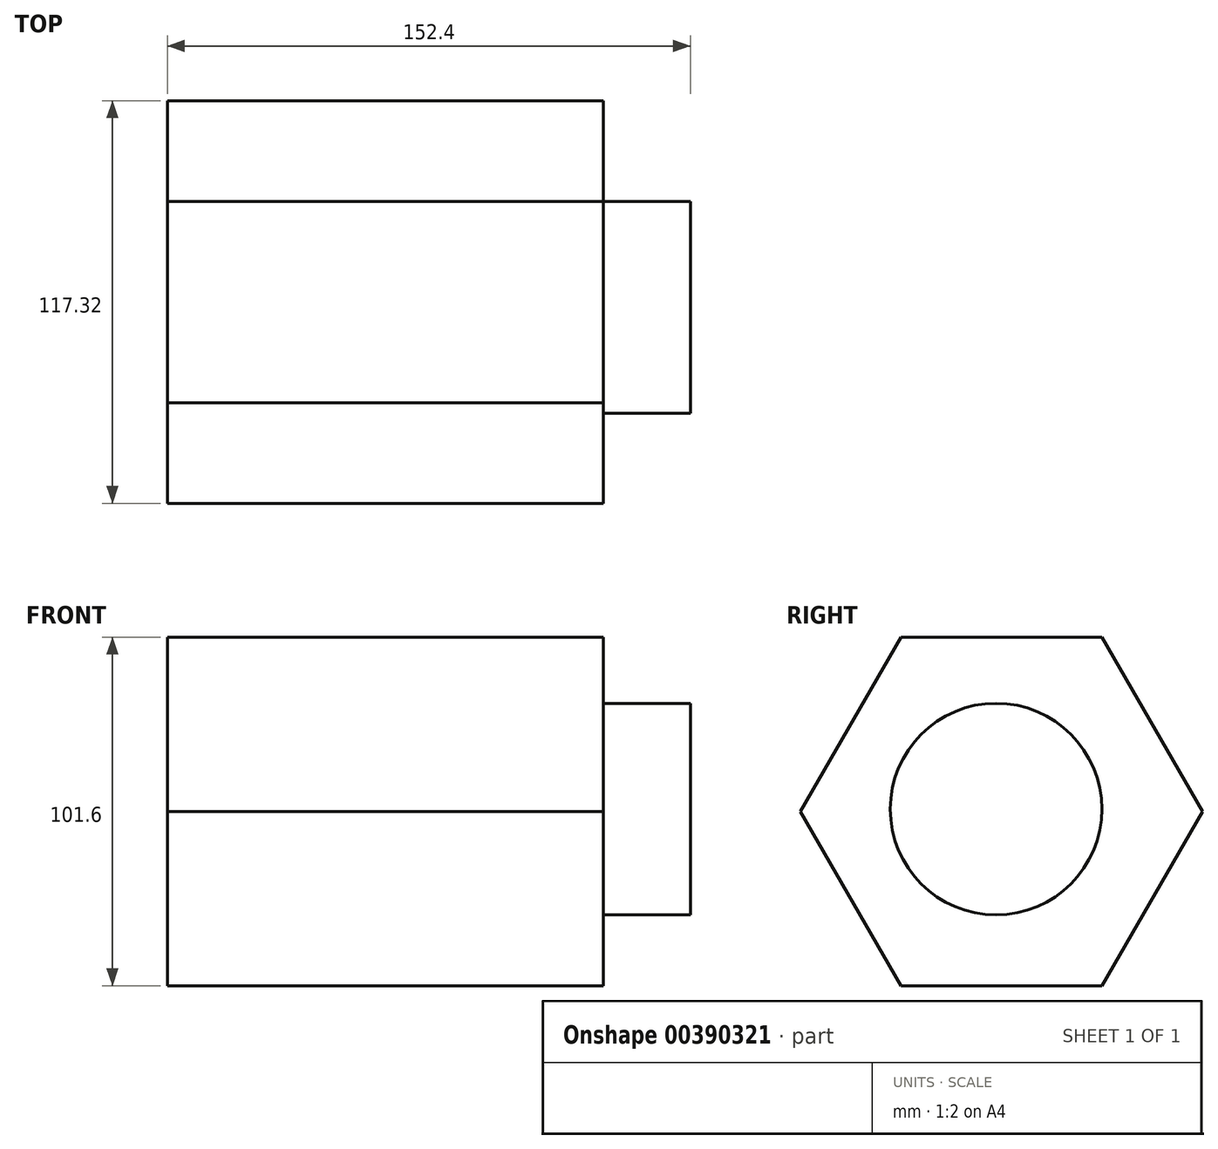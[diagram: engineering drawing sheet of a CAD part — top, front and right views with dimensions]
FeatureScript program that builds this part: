
annotation { "Feature Type Name" : "Feature", "Feature Type Description" : "" }
export const myFeature = defineFeature(function(context is Context, id is Id, definition is map)
    precondition{}
    {
        {
            var Q0;
            Q0=qCreatedBy(makeId("Right.planeOp"),FACE);
            var sketch = newSketch(context, id + "F0", { "sketchPlane" : qUnion([Q0])});
            skCircle(sketch, "E0.cCircle", {"center": v(-33.78, 38.1) * mm, "radius": 50.8 * mm, "construction": true});
            skLineSegment(sketch, "E0.0", {"start": v(-4.45, -12.7) * mm, "end": v(-63.1, -12.7) * mm});
            skLineSegment(sketch, "E0.1", {"start": v(-63.1, -12.7) * mm, "end": v(-92.44, 38.1) * mm});
            skLineSegment(sketch, "E0.2", {"start": v(-92.44, 38.1) * mm, "end": v(-63.1, 88.9) * mm});
            skLineSegment(sketch, "E0.3", {"start": v(-63.1, 88.9) * mm, "end": v(-4.45, 88.9) * mm});
            skLineSegment(sketch, "E0.4", {"start": v(-4.45, 88.9) * mm, "end": v(24.88, 38.1) * mm});
            skLineSegment(sketch, "E0.5", {"start": v(24.88, 38.1) * mm, "end": v(-4.45, -12.7) * mm});
            skPoint(sketch, "E0.0.midPoint", {"position": v(-33.78, -12.7) * mm});
            skSolve(sketch);
        }
        {
            var Q0;
            Q0=makeQuery(id+"F0.imprint","IMPRINT",FACE,{"disambiguationData":[TD([[makeQuery(id+"F0.imprint","IMPRINT",EDGE,{"derivedFrom":sQuery(id+"F0.wireOp",EDGE,"E0.0")}),-1.0]])]});
            extrude(context, id + "F1", {"entities" : qUnion([Q0]), "depth" : 127 * mm});
        }
        {
            var Q0;
            Q0=makeQuery(id+"F1.opExtrude","CAP_FACE",FACE,{"disambiguationData":[OSD([sQuery(id+"F0.wireOp",EDGE,"E0.0"),sQuery(id+"F0.wireOp",EDGE,"E0.1"),sQuery(id+"F0.wireOp",EDGE,"E0.2"),sQuery(id+"F0.wireOp",EDGE,"E0.3"),sQuery(id+"F0.wireOp",EDGE,"E0.4"),sQuery(id+"F0.wireOp",EDGE,"E0.5")])],"isStart":false});
            var sketch = newSketch(context, id + "F2", { "sketchPlane" : qUnion([Q0])});
            skPoint(sketch, "E1", {"position": v(-33.78, 38.1) * mm});
            skPoint(sketch, "E2", {"position": v(-31.7, -59.87) * mm});
            skSolve(sketch);
        }
        {
            var Q0;
            Q0=makeQuery(id+"F2.imprint","IMPRINT",FACE,{"disambiguationData":[TD([[makeQuery(id+"F2.imprint","IMPRINT",EDGE,{"derivedFrom":makeQuery(id+"F1.opExtrude","CAP_EDGE",EDGE,{"disambiguationData":[OSD([sQuery(id+"F0.wireOp",EDGE,"E0.0")])],"isStart":false})}),-1.0]])]});
            var sketch = newSketch(context, id + "F3", { "sketchPlane" : qUnion([Q0])});
            skCircle(sketch, "E3", {"center": v(-36.56, 34.51) * mm, "radius": 9.02 * mm});
            skCircle(sketch, "E4", {"center": v(-36.56, 34.51) * mm, "radius": 2.83 * mm});
            skCircle(sketch, "E5", {"center": v(-36.56, 34.51) * mm, "radius": 5.15 * mm});
            skSolve(sketch);
        }
        {
            var Q0;
            Q0=makeQuery(id+"F2.imprint","IMPRINT",FACE,{"disambiguationData":[TD([[makeQuery(id+"F2.imprint","IMPRINT",EDGE,{"derivedFrom":makeQuery(id+"F1.opExtrude","CAP_EDGE",EDGE,{"disambiguationData":[OSD([sQuery(id+"F0.wireOp",EDGE,"E0.0")])],"isStart":false})}),-1.0]])]});
            var sketch = newSketch(context, id + "F4", { "sketchPlane" : qUnion([Q0])});
            skCircle(sketch, "E6", {"center": v(-35.36, 38.78) * mm, "radius": 30.83 * mm});
            skSolve(sketch);
        }
        {
            var Q0;
            Q0=makeQuery(id+"F4.imprint","IMPRINT",FACE,{"disambiguationData":[TD([[makeQuery(id+"F4.imprint","IMPRINT",EDGE,{"derivedFrom":sQuery(id+"F4.wireOp",EDGE,"E6")}),1.0]])]});
            extrude(context, id + "F5", {"entities" : qUnion([Q0]), "operationType" : NewBodyOperationType.ADD, "depth" : 25.4 * mm});
        }
    });
